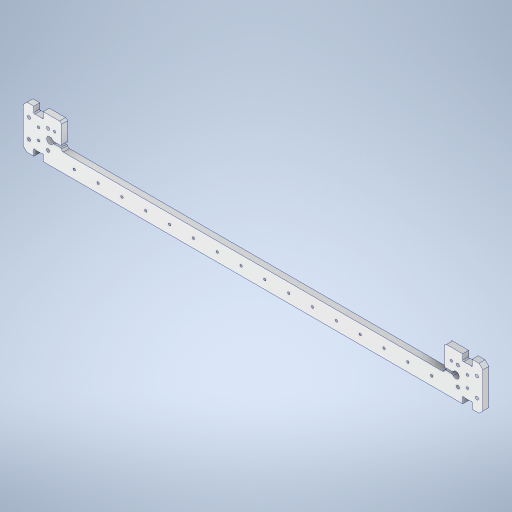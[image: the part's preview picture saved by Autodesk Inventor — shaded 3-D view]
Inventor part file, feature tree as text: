
AUTODESK INVENTOR PART (.ipt)
format: ipt  version: 2024 (Build 280153000, 153)  size: 622,080 bytes
history: native  units: mm
features: sketch x9, mirror x7, extrude x6, projected_geometry x6, hole x4, fillet x3, plane x2, chamfer x1
ambient origin geometry x8: Origin, YZ Plane, XZ Plane, XY Plane, X Axis, Y Axis, Z Axis, Center Point
bodies: Solid1 (feature_tree)
feature tree (38):
  extrude  "Extrusion1"  Depth=45.4mm
  hole  "Hole1"  [1 undecoded]
  extrude  "Extrusion8"  Depth=20.0mm
  hole  "Hole2"  [1 undecoded]
  sketch  "Sketch5"  dims[d12=3.3mm d13=6.0mm d14=4.0mm d15=2.0mm d16=90.0deg d17=8.0mm d18=20.594885mm]
  extrude  "Extrusion9"  Depth=12.0mm
  extrude  "Extrusion4"  Depth=2.0mm
  fillet  "Fillet1"  Radius=10.0mm
  mirror  "Mirror1"
  sketch  "Sketch7"  dims[d32=2.459mm d33=6.0mm d34=4.0mm d35=2.0mm d36=90.0deg d37=8.0mm d38=20.594885mm d46=2.0mm]
  extrude  "Extrusion5"  TaperAngle=0.0deg  [1 undecoded]
  mirror  "Mirror2"
  extrude  "Extrusion7"  Depth=450.0mm
  plane  "Work Plane1"
  mirror  "Mirror3"
  plane  "Work Plane2"
  mirror  "Mirror4"
  mirror  "Mirror5"
  hole  "Hole4"  [1 undecoded]
  mirror  "Mirror6"
  chamfer  "Chamfer1"  Distance=32.4mm
  fillet  "Fillet9"  Radius=6.2mm
  fillet  "Fillet10"  Radius=6.2mm
  hole  "Hole5"  [1 undecoded]
  mirror  "Mirror7"
  sketch  "Sketch1"  dims[d1=27.0mm d2=45.4mm]
  sketch  "Sketch2"  dims[d6=6.35mm d7=0.0mm d8=20.0mm]
  sketch  "Sketch3"  dims[d9=20.0mm d10=20.0mm]
  projected_geometry  "Projected Loop1"
  sketch  "Sketch4"  dims[d11=20.0mm]
  projected_geometry  "Projected Loop3"
  projected_geometry  "Projected Loop5"
  sketch  "Sketch8"  dims[d48=7.0mm d49=12.0mm]
  projected_geometry  "Projected Loop6"
  projected_geometry  "Projected Loop7"
  projected_geometry  "Projected Loop8"
  sketch  "Sketch9"  dims[d54=0.0mm d55=0.0mm d56=2.0mm d69=10.0mm d70=0.0mm]
  sketch  "Sketch10"  dims[d77=1.5mm d80=0.0mm d81=0.0mm d97=450.0mm d98=19.2mm d100=32.4mm d102=6.2mm d103=6.2mm d104=10.0mm d105=0.0mm d106=160.0mm d108=25.0mm d109=10.0mm d111=10.0mm d113=13.5mm d114=12.0mm d115=10.0mm d116=0.0mm d117=9.75mm d118=32.4mm d119=24.0mm d120=20.7mm d121=2.459mm d122=6.0mm d123=4.0mm d124=2.0mm d125=90.0deg d126=8.0mm d127=20.594885mm d128=4.0mm d129=2.0mm d130=45.0deg d131=2.0mm d132=1.0mm d133=12.0mm d134=2.459mm d135=6.0mm d136=4.0mm d137=2.0mm d138=90.0deg d139=8.0mm d140=20.594885mm]
note: 5 required parameter values undecoded (feature->parameter linkage not recoverable at this tier; creation-order binding heuristic only, values carry confidence <= 0.55)
